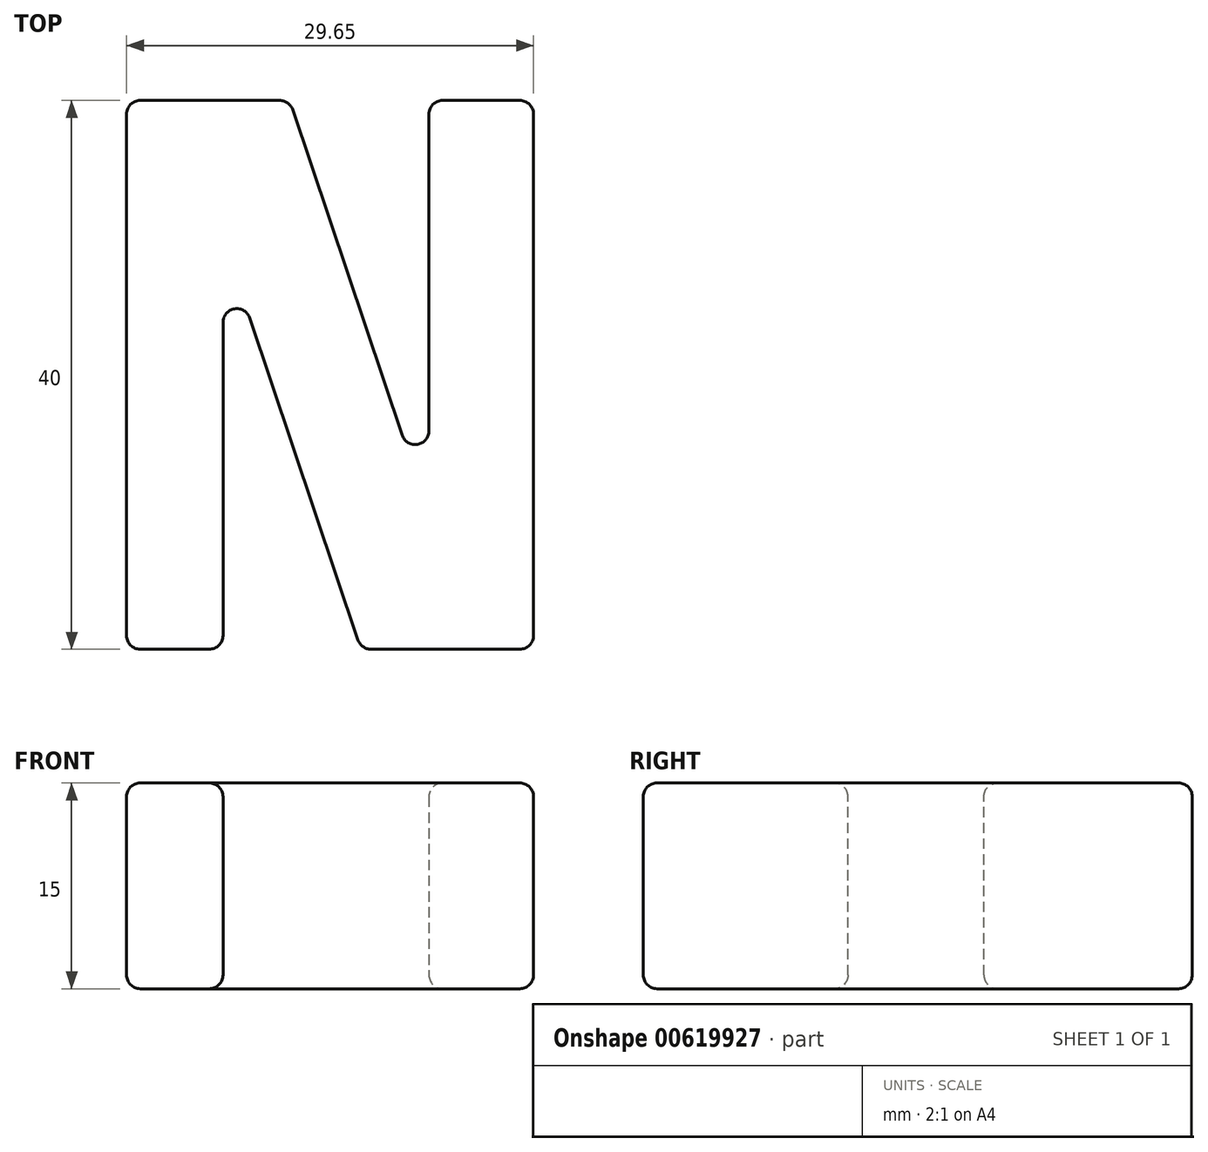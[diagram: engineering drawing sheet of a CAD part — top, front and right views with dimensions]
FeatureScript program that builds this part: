
annotation { "Feature Type Name" : "Feature", "Feature Type Description" : "" }
export const myFeature = defineFeature(function(context is Context, id is Id, definition is map)
    precondition{}
    {
        {
            var Q0;
            Q0=qCreatedBy(makeId("Top.planeOp"),FACE);
            var sketch = newSketch(context, id + "F0", { "sketchPlane" : qUnion([Q0])});
            skLineSegment(sketch, "E0", {"start": v(-40.15, 0) * mm, "end": v(-40.15, 40) * mm});
            skLineSegment(sketch, "E1", {"start": v(-40.15, 40) * mm, "end": v(-28.27, 40) * mm});
            skLineSegment(sketch, "E2", {"start": v(-28.27, 40) * mm, "end": v(-18.12, 9.8) * mm});
            skLineSegment(sketch, "E3", {"start": v(-18.12, 9.8) * mm, "end": v(-18.12, 40) * mm});
            skLineSegment(sketch, "E4", {"start": v(-18.12, 40) * mm, "end": v(-10.5, 40) * mm});
            skLineSegment(sketch, "E5", {"start": v(-10.5, 40) * mm, "end": v(-10.5, 0) * mm});
            skLineSegment(sketch, "E6", {"start": v(-10.5, 0) * mm, "end": v(-23.06, 0) * mm});
            skLineSegment(sketch, "E7", {"start": v(-23.06, 0) * mm, "end": v(-33.13, 29.93) * mm});
            skLineSegment(sketch, "E8", {"start": v(-33.13, 29.93) * mm, "end": v(-33.13, 0) * mm});
            skLineSegment(sketch, "E9", {"start": v(-33.13, 0) * mm, "end": v(-40.15, 0) * mm});
            skSolve(sketch);
        }
        {
            var Q0;
            Q0 = qSketchRegion(id + "F0", true);
            extrude(context, id + "F1", {"entities" : qUnion([Q0]), "depth" : 15 * mm, "offsetDistance" : 25 * mm});
        }
        {
            var Q0;
            Q0=makeQuery(id+"F1.opExtrude","CAP_FACE",FACE,{"disambiguationData":[OSD([sQuery(id+"F0.wireOp",EDGE,"E0"),sQuery(id+"F0.wireOp",EDGE,"E1"),sQuery(id+"F0.wireOp",EDGE,"E2"),sQuery(id+"F0.wireOp",EDGE,"E3"),sQuery(id+"F0.wireOp",EDGE,"E4"),sQuery(id+"F0.wireOp",EDGE,"E5"),sQuery(id+"F0.wireOp",EDGE,"E6"),sQuery(id+"F0.wireOp",EDGE,"E7"),sQuery(id+"F0.wireOp",EDGE,"E8"),sQuery(id+"F0.wireOp",EDGE,"E9")])],"isStart":false});
            var Q1;
            Q1=makeQuery(id+"F1.opExtrude","CAP_FACE",FACE,{"disambiguationData":[OSD([sQuery(id+"F0.wireOp",EDGE,"E0"),sQuery(id+"F0.wireOp",EDGE,"E1"),sQuery(id+"F0.wireOp",EDGE,"E2"),sQuery(id+"F0.wireOp",EDGE,"E3"),sQuery(id+"F0.wireOp",EDGE,"E4"),sQuery(id+"F0.wireOp",EDGE,"E5"),sQuery(id+"F0.wireOp",EDGE,"E6"),sQuery(id+"F0.wireOp",EDGE,"E7"),sQuery(id+"F0.wireOp",EDGE,"E8"),sQuery(id+"F0.wireOp",EDGE,"E9")])],"isStart":true});
            var Q2;
            Q2=makeQuery(id+"F1.opExtrude","SWEPT_FACE",FACE,{"disambiguationData":[OSD([sQuery(id+"F0.wireOp",EDGE,"E6")])]});
            var Q3;
            Q3=makeQuery(id+"F1.opExtrude","SWEPT_FACE",FACE,{"disambiguationData":[OSD([sQuery(id+"F0.wireOp",EDGE,"E9")])]});
            var Q4;
            Q4=makeQuery(id+"F1.opExtrude","SWEPT_FACE",FACE,{"disambiguationData":[OSD([sQuery(id+"F0.wireOp",EDGE,"E1")])]});
            var Q5;
            Q5=makeQuery(id+"F1.opExtrude","SWEPT_FACE",FACE,{"disambiguationData":[OSD([sQuery(id+"F0.wireOp",EDGE,"E4")])]});
            var Q6;
            Q6=makeQuery(id+"F1.opExtrude","SWEPT_EDGE",EDGE,{"disambiguationData":[OSD([sQuery(id+"F0.wireOp",EDGE,"E7"),sQuery(id+"F0.wireOp",EDGE,"E8")])]});
            var Q7;
            Q7=makeQuery(id+"F1.opExtrude","SWEPT_EDGE",EDGE,{"disambiguationData":[OSD([sQuery(id+"F0.wireOp",EDGE,"E2"),sQuery(id+"F0.wireOp",EDGE,"E3")])]});
            fillet(context, id + "F2", {"entities" : qUnion([Q0, Q1, Q2, Q3, Q4, Q5, Q6, Q7]), "radius" : 1 * mm, "tangentPropagation" : true, "allowEdgeOverflow" : false});
        }
    });
